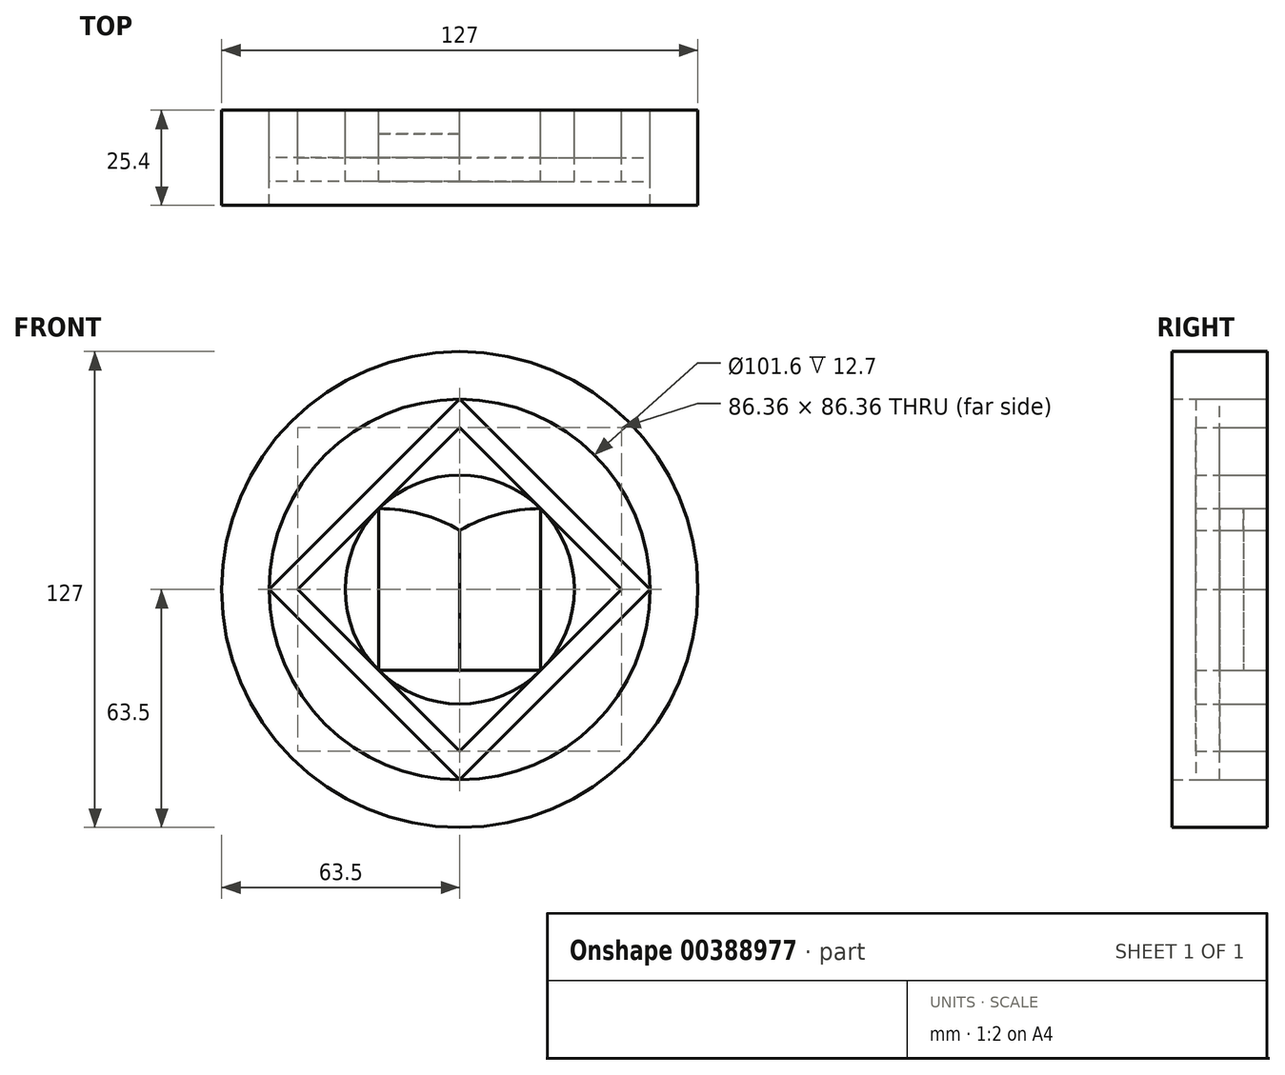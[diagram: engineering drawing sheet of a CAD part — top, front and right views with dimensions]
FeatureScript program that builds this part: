
annotation { "Feature Type Name" : "Feature", "Feature Type Description" : "" }
export const myFeature = defineFeature(function(context is Context, id is Id, definition is map)
    precondition{}
    {
        {
            var Q0;
            Q0=qCreatedBy(makeId("Front.planeOp"),FACE);
            var sketch = newSketch(context, id + "F0", { "sketchPlane" : qUnion([Q0])});
            skCircle(sketch, "E0", {"center": v(0, 0) * mm, "radius": 63.5 * mm});
            skCircle(sketch, "E1", {"center": v(0, 0) * mm, "radius": 50.8 * mm});
            skLineSegment(sketch, "E2", {"start": v(-50.8, 0) * mm, "end": v(0, -50.8) * mm});
            skLineSegment(sketch, "E3", {"start": v(0, -50.8) * mm, "end": v(50.8, 0) * mm});
            skLineSegment(sketch, "E4", {"start": v(50.8, 0) * mm, "end": v(0, 50.8) * mm});
            skLineSegment(sketch, "E5", {"start": v(0, 50.8) * mm, "end": v(-50.8, 0) * mm});
            skLineSegment(sketch, "E6", {"start": v(-43.18, 0) * mm, "end": v(0, 43.18) * mm});
            skLineSegment(sketch, "E7", {"start": v(0, 43.18) * mm, "end": v(43.18, 0) * mm});
            skLineSegment(sketch, "E8", {"start": v(43.18, 0) * mm, "end": v(0, -43.18) * mm});
            skLineSegment(sketch, "E9", {"start": v(0, -43.18) * mm, "end": v(-43.18, 0) * mm});
            skCircle(sketch, "E10", {"center": v(0, 0) * mm, "radius": 30.53 * mm});
            skLineSegment(sketch, "E11", {"start": v(-21.59, 21.6) * mm, "end": v(-21.59, -21.59) * mm});
            skLineSegment(sketch, "E12", {"start": v(-21.59, -21.59) * mm, "end": v(21.6, -21.59) * mm});
            skLineSegment(sketch, "E13", {"start": v(21.6, -21.59) * mm, "end": v(21.6, 21.6) * mm});
            skLineSegment(sketch, "E14", {"start": v(0, 15.8) * mm, "end": v(0, -21.59) * mm});
            skArc(sketch, "E15.trimOffspring", {"start": v(0, 15.8) * mm, "mid": v(-10.41, 20.12) * mm, "end": v(-21.59, 21.6) * mm});
            skArc(sketch, "E16.trimOffspring", {"start": v(21.6, 21.6) * mm, "mid": v(10.41, 20.12) * mm, "end": v(0, 15.8) * mm});
            skLineSegment(sketch, "E17", {"start": v(-50.8, 0) * mm, "end": v(-43.18, 0) * mm});
            skLineSegment(sketch, "E18", {"start": v(0, -43.18) * mm, "end": v(0, -50.8) * mm});
            skLineSegment(sketch, "E19", {"start": v(43.18, 0) * mm, "end": v(50.8, 0) * mm});
            skLineSegment(sketch, "E20", {"start": v(0, 43.18) * mm, "end": v(0, 50.8) * mm});
            skSolve(sketch);
        }
        {
            var Q0;
            Q0=makeQuery(id+"F0.imprint","IMPRINT",FACE,{"disambiguationData":[TD([[makeQuery(id+"F0.imprint","IMPRINT",EDGE,{"derivedFrom":sQuery(id+"F0.wireOp",EDGE,"E0")}),1.0]])]});
            extrude(context, id + "F1", {"entities" : qUnion([Q0]), "depth" : 25.4 * mm});
        }
        {
            var Q0;
            {var subQ0=sQuery(id+"F0.wireOp",EDGE,"E5");Q0=makeQuery(id+"F0.imprint","IMPRINT",FACE,{"disambiguationData":[TD([[makeQuery(id+"F0.imprint","IMPRINT",EDGE,{"derivedFrom":subQ0}),-1.0]])]});}
            var Q1;
            {var subQ0=sQuery(id+"F0.wireOp",EDGE,"E2");Q1=makeQuery(id+"F0.imprint","IMPRINT",FACE,{"disambiguationData":[TD([[makeQuery(id+"F0.imprint","IMPRINT",EDGE,{"derivedFrom":subQ0}),-1.0]])]});}
            var Q2;
            {var subQ0=sQuery(id+"F0.wireOp",EDGE,"E3");Q2=makeQuery(id+"F0.imprint","IMPRINT",FACE,{"disambiguationData":[TD([[makeQuery(id+"F0.imprint","IMPRINT",EDGE,{"derivedFrom":subQ0}),-1.0]])]});}
            var Q3;
            {var subQ0=sQuery(id+"F0.wireOp",EDGE,"E4");Q3=makeQuery(id+"F0.imprint","IMPRINT",FACE,{"disambiguationData":[TD([[makeQuery(id+"F0.imprint","IMPRINT",EDGE,{"derivedFrom":subQ0}),-1.0]])]});}
            extrude(context, id + "F2", {"entities" : qUnion([Q0, Q1, Q2, Q3]), "operationType" : NewBodyOperationType.ADD, "depth" : 12.7 * mm});
        }
        {
            var Q0;
            {var subQ0=sQuery(id+"F0.wireOp",EDGE,"E9");var subQ1=sQuery(id+"F0.wireOp",EDGE,"E6");var subQ2=makeQuery(id+"F0.imprint","INTERSECT",VERTEX,{"derivedFrom":[subQ1,subQ0,sQuery(id+"F0.wireOp",EDGE,"E17")]});Q0=makeQuery(id+"F0.imprint","IMPRINT",FACE,{"disambiguationData":[TD([[makeQuery(id+"F0.imprint","IMPRINT",EDGE,{"disambiguationData":[TD([[subQ2,-1.0]])],"derivedFrom":subQ1}),-1.0]])]});}
            var Q1;
            {var subQ0=sQuery(id+"F0.wireOp",EDGE,"E9");var subQ1=sQuery(id+"F0.wireOp",EDGE,"E8");var subQ2=makeQuery(id+"F0.imprint","INTERSECT",VERTEX,{"derivedFrom":[subQ1,subQ0,sQuery(id+"F0.wireOp",EDGE,"E18")]});Q1=makeQuery(id+"F0.imprint","IMPRINT",FACE,{"disambiguationData":[TD([[makeQuery(id+"F0.imprint","IMPRINT",EDGE,{"disambiguationData":[TD([[subQ2,1.0]])],"derivedFrom":subQ1}),-1.0]])]});}
            var Q2;
            {var subQ0=sQuery(id+"F0.wireOp",EDGE,"E8");var subQ1=sQuery(id+"F0.wireOp",EDGE,"E7");var subQ2=makeQuery(id+"F0.imprint","INTERSECT",VERTEX,{"derivedFrom":[subQ1,subQ0,sQuery(id+"F0.wireOp",EDGE,"E19")]});Q2=makeQuery(id+"F0.imprint","IMPRINT",FACE,{"disambiguationData":[TD([[makeQuery(id+"F0.imprint","IMPRINT",EDGE,{"disambiguationData":[TD([[subQ2,1.0]])],"derivedFrom":subQ1}),-1.0]])]});}
            var Q3;
            {var subQ0=sQuery(id+"F0.wireOp",EDGE,"E7");var subQ1=sQuery(id+"F0.wireOp",EDGE,"E6");var subQ2=makeQuery(id+"F0.imprint","INTERSECT",VERTEX,{"derivedFrom":[subQ1,subQ0,sQuery(id+"F0.wireOp",EDGE,"E20")]});Q3=makeQuery(id+"F0.imprint","IMPRINT",FACE,{"disambiguationData":[TD([[makeQuery(id+"F0.imprint","IMPRINT",EDGE,{"disambiguationData":[TD([[subQ2,1.0]])],"derivedFrom":subQ1}),-1.0]])]});}
            extrude(context, id + "F3", {"entities" : qUnion([Q0, Q1, Q2, Q3]), "depth" : 12.7 * mm});
        }
        {
            var Q0;
            {var subQ0=sQuery(id+"F0.wireOp",EDGE,"E15.trimOffspring");Q0=makeQuery(id+"F0.imprint","IMPRINT",FACE,{"disambiguationData":[TD([[makeQuery(id+"F0.imprint","IMPRINT",EDGE,{"derivedFrom":subQ0}),-1.0]])]});}
            var Q1;
            {var subQ0=sQuery(id+"F0.wireOp",EDGE,"E11");Q1=makeQuery(id+"F0.imprint","IMPRINT",FACE,{"disambiguationData":[TD([[makeQuery(id+"F0.imprint","IMPRINT",EDGE,{"derivedFrom":subQ0}),-1.0]])]});}
            var Q2;
            {var subQ0=sQuery(id+"F0.wireOp",EDGE,"E13");Q2=makeQuery(id+"F0.imprint","IMPRINT",FACE,{"disambiguationData":[TD([[makeQuery(id+"F0.imprint","IMPRINT",EDGE,{"derivedFrom":subQ0}),-1.0]])]});}
            var Q3;
            {var subQ0=sQuery(id+"F0.wireOp",EDGE,"E12");var subQ4=makeQuery(id+"F0.imprint","INTERSECT",VERTEX,{"derivedFrom":[subQ0,sQuery(id+"F0.wireOp",EDGE,"E14")]});Q3=makeQuery(id+"F0.imprint","IMPRINT",FACE,{"disambiguationData":[TD([[makeQuery(id+"F0.imprint","IMPRINT",EDGE,{"disambiguationData":[TD([[subQ4,1.0]])],"derivedFrom":subQ0}),-1.0]])]});}
            extrude(context, id + "F4", {"entities" : qUnion([Q0, Q1, Q2, Q3]), "depth" : 19.05 * mm});
        }
        {
            var Q0;
            Q0=makeQuery(id+"F0.imprint","IMPRINT",FACE,{"disambiguationData":[TD([[makeQuery(id+"F0.imprint","IMPRINT",EDGE,{"derivedFrom":sQuery(id+"F0.wireOp",EDGE,"E2")}),1.0]])]});
            var Q1;
            Q1=makeQuery(id+"F0.imprint","IMPRINT",FACE,{"disambiguationData":[TD([[makeQuery(id+"F0.imprint","IMPRINT",EDGE,{"derivedFrom":sQuery(id+"F0.wireOp",EDGE,"E5")}),1.0]])]});
            var Q2;
            Q2=makeQuery(id+"F0.imprint","IMPRINT",FACE,{"disambiguationData":[TD([[makeQuery(id+"F0.imprint","IMPRINT",EDGE,{"derivedFrom":sQuery(id+"F0.wireOp",EDGE,"E3")}),1.0]])]});
            var Q3;
            Q3=makeQuery(id+"F0.imprint","IMPRINT",FACE,{"disambiguationData":[TD([[makeQuery(id+"F0.imprint","IMPRINT",EDGE,{"derivedFrom":sQuery(id+"F0.wireOp",EDGE,"E4")}),1.0]])]});
            extrude(context, id + "F5", {"entities" : qUnion([Q0, Q1, Q2, Q3]), "depth" : 19.05 * mm});
        }
        {
            var Q0;
            {var subQ0=sQuery(id+"F0.wireOp",EDGE,"E11");Q0=makeQuery(id+"F0.imprint","IMPRINT",FACE,{"disambiguationData":[TD([[makeQuery(id+"F0.imprint","IMPRINT",EDGE,{"derivedFrom":subQ0}),1.0]])]});}
            extrude(context, id + "F6", {"entities" : qUnion([Q0]), "depth" : 6.35 * mm});
        }
        {
            var Q0;
            {var subQ0=sQuery(id+"F0.wireOp",EDGE,"E13");Q0=makeQuery(id+"F0.imprint","IMPRINT",FACE,{"disambiguationData":[TD([[makeQuery(id+"F0.imprint","IMPRINT",EDGE,{"derivedFrom":subQ0}),1.0]])]});}
            extrude(context, id + "F7", {"entities" : qUnion([Q0]), "depth" : 12.7 * mm});
        }
    });
